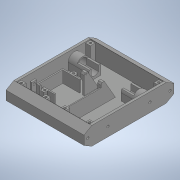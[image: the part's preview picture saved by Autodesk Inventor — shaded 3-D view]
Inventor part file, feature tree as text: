
AUTODESK INVENTOR PART (.ipt)
format: ipt  version: 2020 (Build 240168000, 168)  size: 632,320 bytes
history: native  units: in
note: dims shown in document units (in); Inventor stores cm internally (conversion verified against a paired STEP export)
features: extrude x18, sketch x18, projected_geometry x14, mirror x6, plane x1
ambient origin geometry x8: Origin, YZ Plane, XZ Plane, XY Plane, X Axis, Y Axis, Z Axis, Center Point
bodies: Solid1 (feature_tree)
feature tree (57):
  extrude  "Extrusion1"  Depth=5.9055in
  extrude  "Extrusion2"  TaperAngle=0.0deg  [1 undecoded]
  extrude  "Extrusion3"  Depth=1.063in
  extrude  "Extrusion4"  Depth=0.315in
  extrude  "Extrusion5"  TaperAngle=0.0deg  [1 undecoded]
  extrude  "Extrusion6"  Depth=0.5906in
  mirror  "Mirror1"
  extrude  "Extrusion7"  Depth=0.0787in
  mirror  "Mirror2"
  extrude  "Extrusion8"  Depth=0.6102in
  mirror  "Mirror3"
  plane  "Work Plane1"
  extrude  "Extrusion9"  Depth=0.7874in TaperAngle=0.0deg
  mirror  "Mirror4"
  extrude  "Extrusion10"  Depth=6.063in TaperAngle=0.0deg
  extrude  "Extrusion11"  Depth=0.1575in
  extrude  "Extrusion12"  TaperAngle=0.0deg  [1 undecoded]
  extrude  "Extrusion13"  Depth=0.2756in
  extrude  "Extrusion14"  Depth=0.4331in
  extrude  "Extrusion17"  Depth=2.7559in
  extrude  "Extrusion18"  Depth=0.0413in
  mirror  "Mirror6"
  extrude  "Extrusion19"  TaperAngle=0.0deg  [1 undecoded]
  mirror  "Mirror7"
  extrude  "Extrusion20"  Depth=0.0787in
  sketch  "Sketch1"  dims[d0=1.1811in d1=5.9055in]
  sketch  "Sketch2"  dims[d2=5.1181in d3=0.0in]
  projected_geometry  "Projected Loop1"
  sketch  "Sketch3"  dims[d4=0.1575in d5=1.063in]
  projected_geometry  "Projected Loop2"
  projected_geometry  "Projected Loop3"
  sketch  "Sketch4"  dims[d6=0.0in d8=0.315in]
  sketch  "Sketch5"  dims[d10=0.993in d11=0.0in]
  projected_geometry  "Projected Loop4"
  sketch  "Sketch6"  dims[d12=0.6496in d13=0.5906in]
  sketch  "Sketch7"  dims[d14=1.5748in d15=0.0787in]
  sketch  "Sketch9"  dims[d16=0.5512in d17=0.0in d18=0.6102in]
  sketch  "Sketch10"  dims[d19=0.4803in d20=0.7874in d21=0.0in]
  sketch  "Sketch12"  dims[d22=0.1654in d23=6.063in d24=0.0in]
  projected_geometry  "Projected Loop6"
  projected_geometry  "Projected Loop7"
  projected_geometry  "Projected Loop8"
  sketch  "Sketch13"  dims[d25=0.5114in d26=0.1575in]
  sketch  "Sketch14"  dims[d27=1.5748in d28=0.0in d29=0.0in]
  sketch  "Sketch15"  dims[d30=0.1575in d31=0.2756in]
  projected_geometry  "Projected Loop15"
  sketch  "Sketch16"  dims[d32=0.0in d33=0.4331in]
  projected_geometry  "Projected Loop19"
  projected_geometry  "Projected Loop20"
  projected_geometry  "Projected Loop21"
  projected_geometry  "Projected Loop22"
  projected_geometry  "Projected Loop23"
  projected_geometry  "Projected Loop24"
  sketch  "Sketch20"  dims[d34=0.0827in d38=2.7559in]
  sketch  "Sketch21"  dims[d40=0.0413in d41=0.0909in]
  sketch  "Sketch22"  dims[d42=0.2362in d43=0.0in]
  sketch  "Sketch23"  dims[d44=60.0deg d45=0.0787in d46=0.315in d48=0.993in d49=0.0in d53=0.2756in d54=0.0in d55=0.4724in d56=1.1811in d57=1.5748in d58=1.5748in d59=0.0787in d60=0.0787in d62=0.315in d63=0.7677in d64=0.0in d66=0.1476in d67=0.2756in d68=0.0in d69=0.7874in d70=0.2953in d71=0.1181in d72=0.0in d89=0.0157in d90=0.0157in d91=0.1476in d92=0.1476in d96=0.315in d97=0.1575in d98=0.1181in d99=0.0in d102=0.1772in d104=0.3346in d105=135.0deg d106=0.2362in d107=0.0in d108=0.0394in d109=0.0in d110=0.063in d111=0.0394in d112=0.0in]
note: 4 required parameter values undecoded (feature->parameter linkage not recoverable at this tier; creation-order binding heuristic only, values carry confidence <= 0.55)
